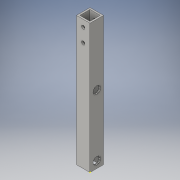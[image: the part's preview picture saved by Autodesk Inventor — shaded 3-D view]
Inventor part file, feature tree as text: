
AUTODESK INVENTOR PART (.ipt)
format: ipt  version: 2016 (Build 200138000, 138)  size: 261,120 bytes
history: native  units: in
note: dims shown in document units (in); Inventor stores cm internally (conversion verified against a paired STEP export)
features: sketch x10, extrude x9
ambient origin geometry x8: Origin, YZ Plane, XZ Plane, XY Plane, X Axis, Y Axis, Z Axis, Center Point
bodies: Solid1 (feature_tree)
feature tree (19):
  extrude  "Extrusion1"  Depth=1.0in
  extrude  "Extrusion2"  Depth=0.5in
  extrude  "Extrusion3"  Depth=0.125in
  sketch  "Sketch4"  dims[d8=9.0in d9=0.0in d11=2.0in]
  extrude  "Extrusion4"  Depth=2.0in
  extrude  "Extrusion5"  Depth=0.125in
  extrude  "Extrusion6"  Depth=1.0in
  extrude  "Extrusion7"  Depth=0.125in
  extrude  "Extrusion8"  Depth=1.0in TaperAngle=0.0deg
  extrude  "Extrusion9"  Depth=0.5in
  sketch  "Sketch1"  dims[d0=9.5in d1=1.0in]
  sketch  "Sketch2"  dims[d3=0.5in d4=0.5in]
  sketch  "Sketch3"  dims[d5=1.0in d6=0.0in d7=0.125in]
  sketch  "Sketch5"  dims[d13=0.125in d15=0.125in]
  sketch  "Sketch6"  dims[d16=1.0in d17=0.0in d18=1.75in]
  sketch  "Sketch7"  dims[d19=1.5in d20=0.125in]
  sketch  "Sketch8"  dims[d21=0.125in d22=1.0in d23=0.0in]
  sketch  "Sketch9"  dims[d25=0.5in d26=0.5in]
  sketch  "Sketch10"  dims[d27=0.5in d28=1.0in d29=0.0in d30=1.0in d31=0.0in d32=1.0in d33=0.0in d34=0.5in d35=5.0in d36=0.5in d37=1.0in d38=0.0in d39=0.25in d40=0.25in d41=0.5in d42=1.5in d43=1.0in d44=0.0in]
